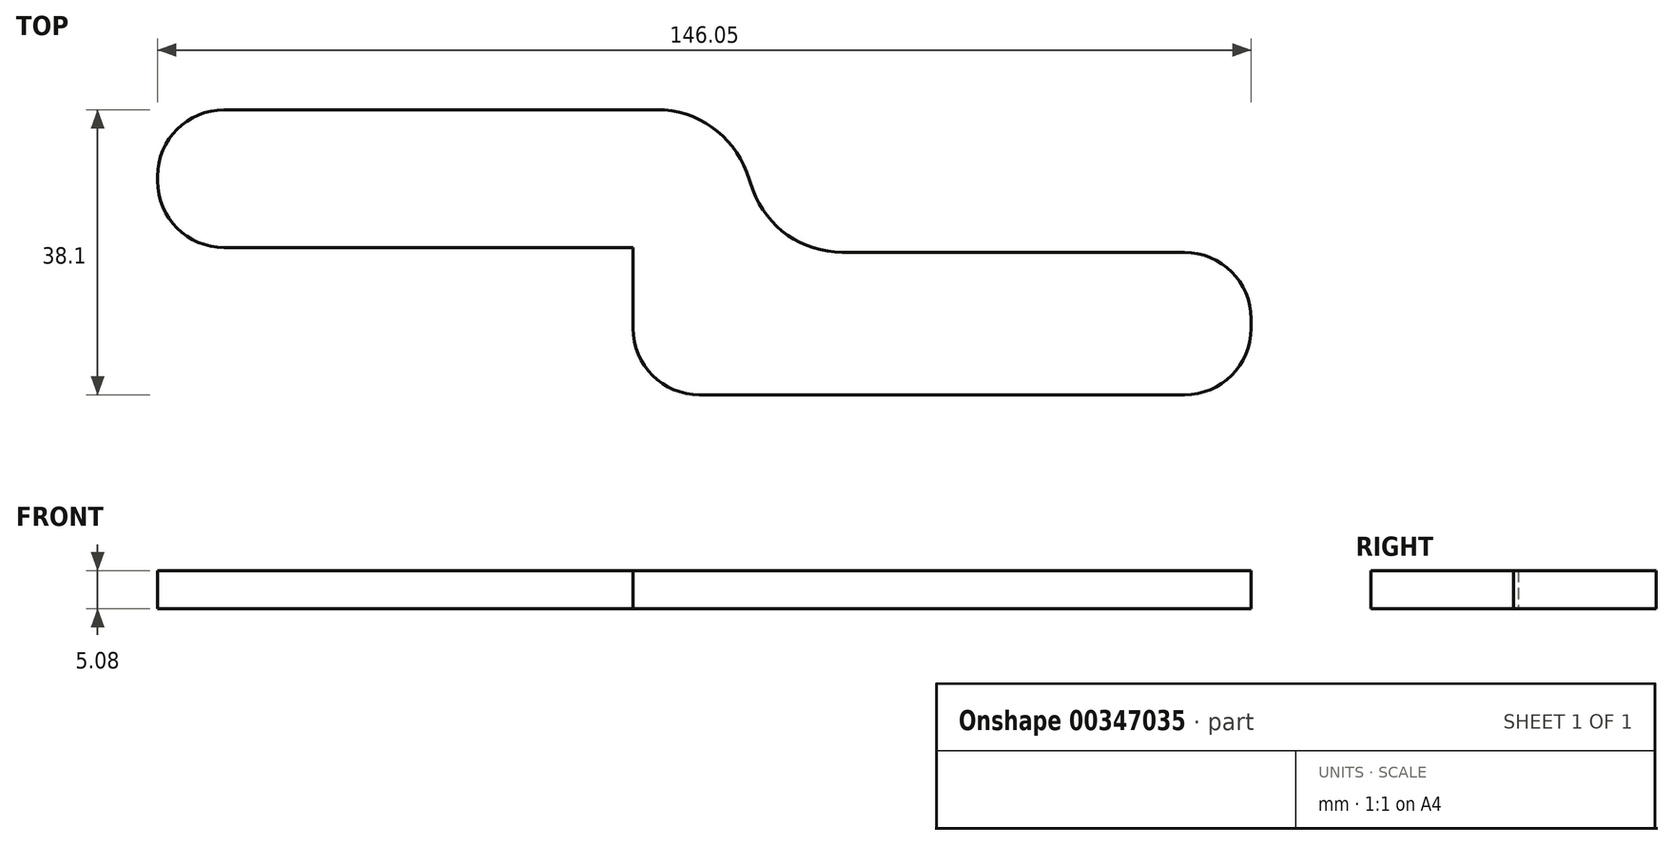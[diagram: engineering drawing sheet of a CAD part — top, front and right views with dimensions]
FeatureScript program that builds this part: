
annotation { "Feature Type Name" : "Feature", "Feature Type Description" : "" }
export const myFeature = defineFeature(function(context is Context, id is Id, definition is map)
    precondition{}
    {
        {
            var Q0;
            Q0=qCreatedBy(makeId("Top.planeOp"),FACE);
            var sketch = newSketch(context, id + "F0", { "sketchPlane" : qUnion([Q0])});
            skLineSegment(sketch, "E0", {"start": v(-54.6, 0) * mm, "end": v(0, 0) * mm});
            skLineSegment(sketch, "E1", {"start": v(0, 0) * mm, "end": v(0, -10.8) * mm});
            skLineSegment(sketch, "E2", {"start": v(8.9, -19.68) * mm, "end": v(73.66, -19.68) * mm});
            skLineSegment(sketch, "E3", {"start": v(82.55, -10.8) * mm, "end": v(82.55, -9.52) * mm});
            skLineSegment(sketch, "E4", {"start": v(73.66, -0.63) * mm, "end": v(27.94, -0.63) * mm});
            skLineSegment(sketch, "E5", {"start": v(3.22, 18.42) * mm, "end": v(-54.6, 18.42) * mm});
            skLineSegment(sketch, "E6", {"start": v(-63.5, 9.53) * mm, "end": v(-63.5, 8.89) * mm});
            skPoint(sketch, "E7.visualSharp", {"position": v(-63.5, 18.42) * mm});
            skArc(sketch, "E7.filletArc", {"start": v(-54.6, 18.42) * mm, "mid": v(-60.9, 15.81) * mm, "end": v(-63.5, 9.53) * mm});
            skPoint(sketch, "E8.visualSharp", {"position": v(-63.5, 0) * mm});
            skArc(sketch, "E8.filletArc", {"start": v(-63.5, 8.89) * mm, "mid": v(-60.9, 2.6) * mm, "end": v(-54.6, 0) * mm});
            skPoint(sketch, "E9.visualSharp", {"position": v(0, -19.68) * mm});
            skArc(sketch, "E9.filletArc", {"start": v(0, -10.8) * mm, "mid": v(2.6, -17.08) * mm, "end": v(8.9, -19.68) * mm});
            skPoint(sketch, "E10.visualSharp", {"position": v(82.55, -0.63) * mm});
            skArc(sketch, "E10.filletArc", {"start": v(82.55, -9.52) * mm, "mid": v(79.95, -3.24) * mm, "end": v(73.66, -0.63) * mm});
            skPoint(sketch, "E11.visualSharp", {"position": v(82.55, -19.68) * mm});
            skArc(sketch, "E11.filletArc", {"start": v(73.66, -19.68) * mm, "mid": v(79.95, -17.08) * mm, "end": v(82.55, -10.8) * mm});
            skLineSegment(sketch, "E12", {"start": v(15.16, 10.06) * mm, "end": v(16, 7.72) * mm});
            skPoint(sketch, "E13.visualSharp", {"position": v(12.12, 18.42) * mm});
            skArc(sketch, "E13.filletArc", {"start": v(15.16, 10.06) * mm, "mid": v(10.5, 16.12) * mm, "end": v(3.22, 18.42) * mm});
            skPoint(sketch, "E14.visualSharp", {"position": v(19.05, -0.63) * mm});
            skArc(sketch, "E14.filletArc", {"start": v(16, 7.72) * mm, "mid": v(20.66, 1.66) * mm, "end": v(27.94, -0.63) * mm});
            skSolve(sketch);
        }
        {
            var Q0;
            Q0=makeQuery(id+"F0.imprint","IMPRINT",FACE,{"disambiguationData":[TD([[makeQuery(id+"F0.imprint","IMPRINT",EDGE,{"derivedFrom":sQuery(id+"F0.wireOp",EDGE,"E0")}),1.0]])]});
            extrude(context, id + "F1", {"entities" : qUnion([Q0]), "endBound" : BoundingType.SYMMETRIC, "depth" : 5.08 * mm});
        }
    });
